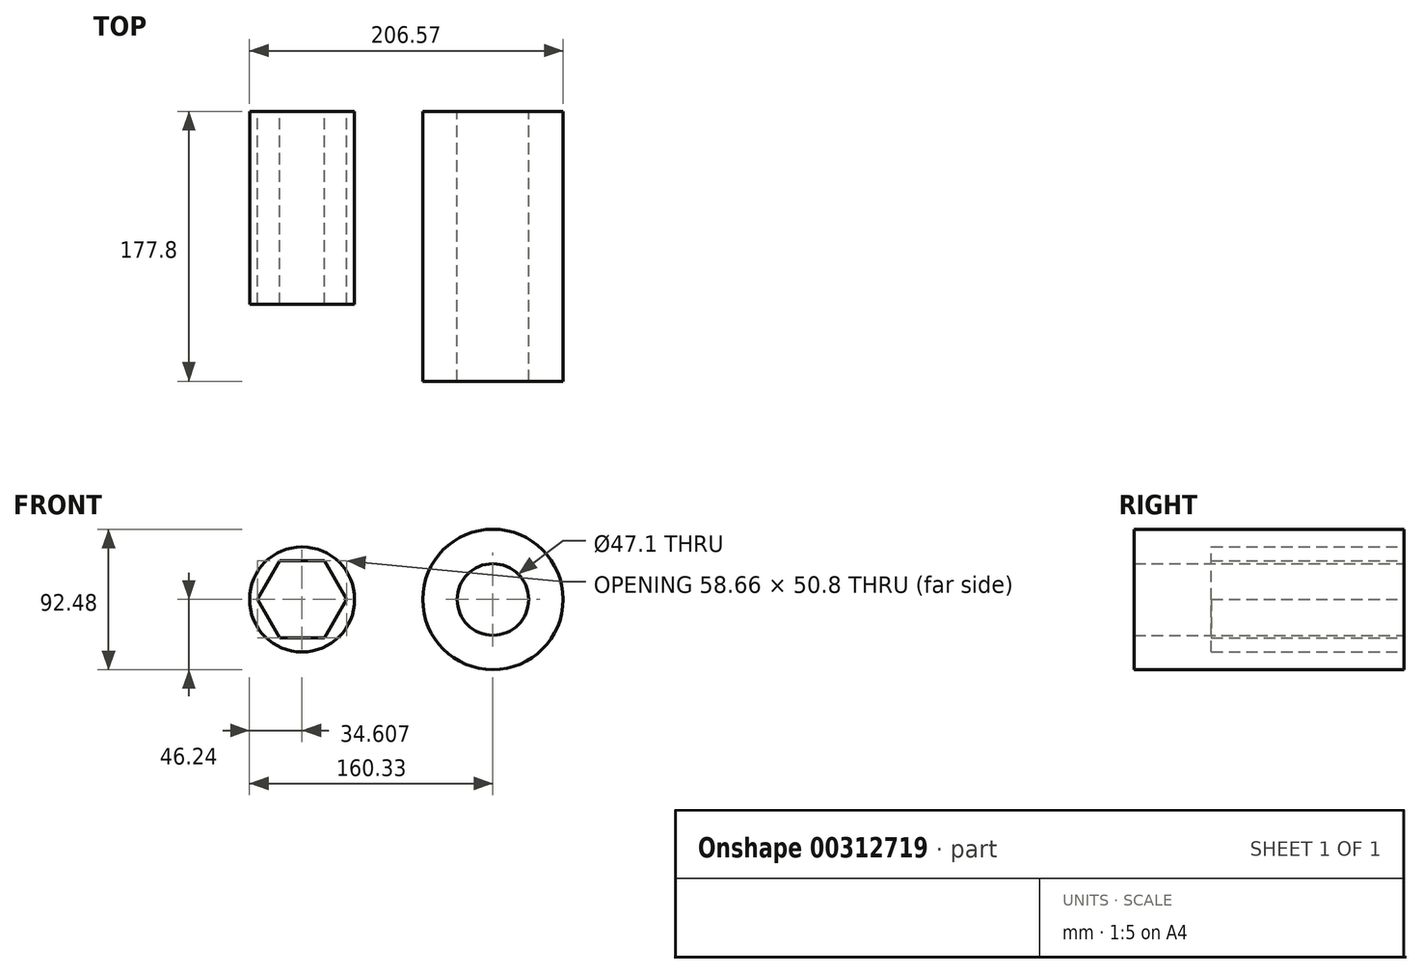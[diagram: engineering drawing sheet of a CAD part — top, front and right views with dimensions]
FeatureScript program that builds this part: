
annotation { "Feature Type Name" : "Feature", "Feature Type Description" : "" }
export const myFeature = defineFeature(function(context is Context, id is Id, definition is map)
    precondition{}
    {
        {
            var Q0;
            Q0=qCreatedBy(makeId("Front.planeOp"),FACE);
            var sketch = newSketch(context, id + "F0", { "sketchPlane" : qUnion([Q0])});
            skCircle(sketch, "E0", {"center": v(0, 0) * mm, "radius": 46.24 * mm});
            skCircle(sketch, "E1", {"center": v(0, 0) * mm, "radius": 23.55 * mm});
            skSolve(sketch);
        }
        {
            var Q0;
            Q0 = qSketchRegion(id + "F0", true);
            extrude(context, id + "F1", {"entities" : qUnion([Q0]), "depth" : 177.8 * mm});
        }
        {
            var Q0;
            Q0=qCreatedBy(makeId("Front.planeOp"),FACE);
            var sketch = newSketch(context, id + "F2", { "sketchPlane" : qUnion([Q0])});
            skCircle(sketch, "E2", {"center": v(-125.72, 0) * mm, "radius": 34.6 * mm});
            skCircle(sketch, "E3.cCircle", {"center": v(-125.72, 0) * mm, "radius": 25.4 * mm, "construction": true});
            skLineSegment(sketch, "E3.0", {"start": v(-111.06, -25.4) * mm, "end": v(-140.39, -25.4) * mm});
            skLineSegment(sketch, "E3.1", {"start": v(-140.39, -25.4) * mm, "end": v(-155.05, 0) * mm});
            skLineSegment(sketch, "E3.2", {"start": v(-155.05, 0) * mm, "end": v(-140.39, 25.4) * mm});
            skLineSegment(sketch, "E3.3", {"start": v(-140.39, 25.4) * mm, "end": v(-111.06, 25.4) * mm});
            skLineSegment(sketch, "E3.4", {"start": v(-111.06, 25.4) * mm, "end": v(-96.4, 0) * mm});
            skLineSegment(sketch, "E3.5", {"start": v(-96.4, 0) * mm, "end": v(-111.06, -25.4) * mm});
            skPoint(sketch, "E3.0.midPoint", {"position": v(-125.72, -25.4) * mm});
            skSolve(sketch);
        }
        {
            var Q0;
            Q0=makeQuery(id+"F2.imprint","IMPRINT",FACE,{"disambiguationData":[TD([[makeQuery(id+"F2.imprint","IMPRINT",EDGE,{"derivedFrom":sQuery(id+"F2.wireOp",EDGE,"E2")}),1.0]])]});
            extrude(context, id + "F3", {"entities" : qUnion([Q0]), "depth" : 127 * mm});
        }
    });
